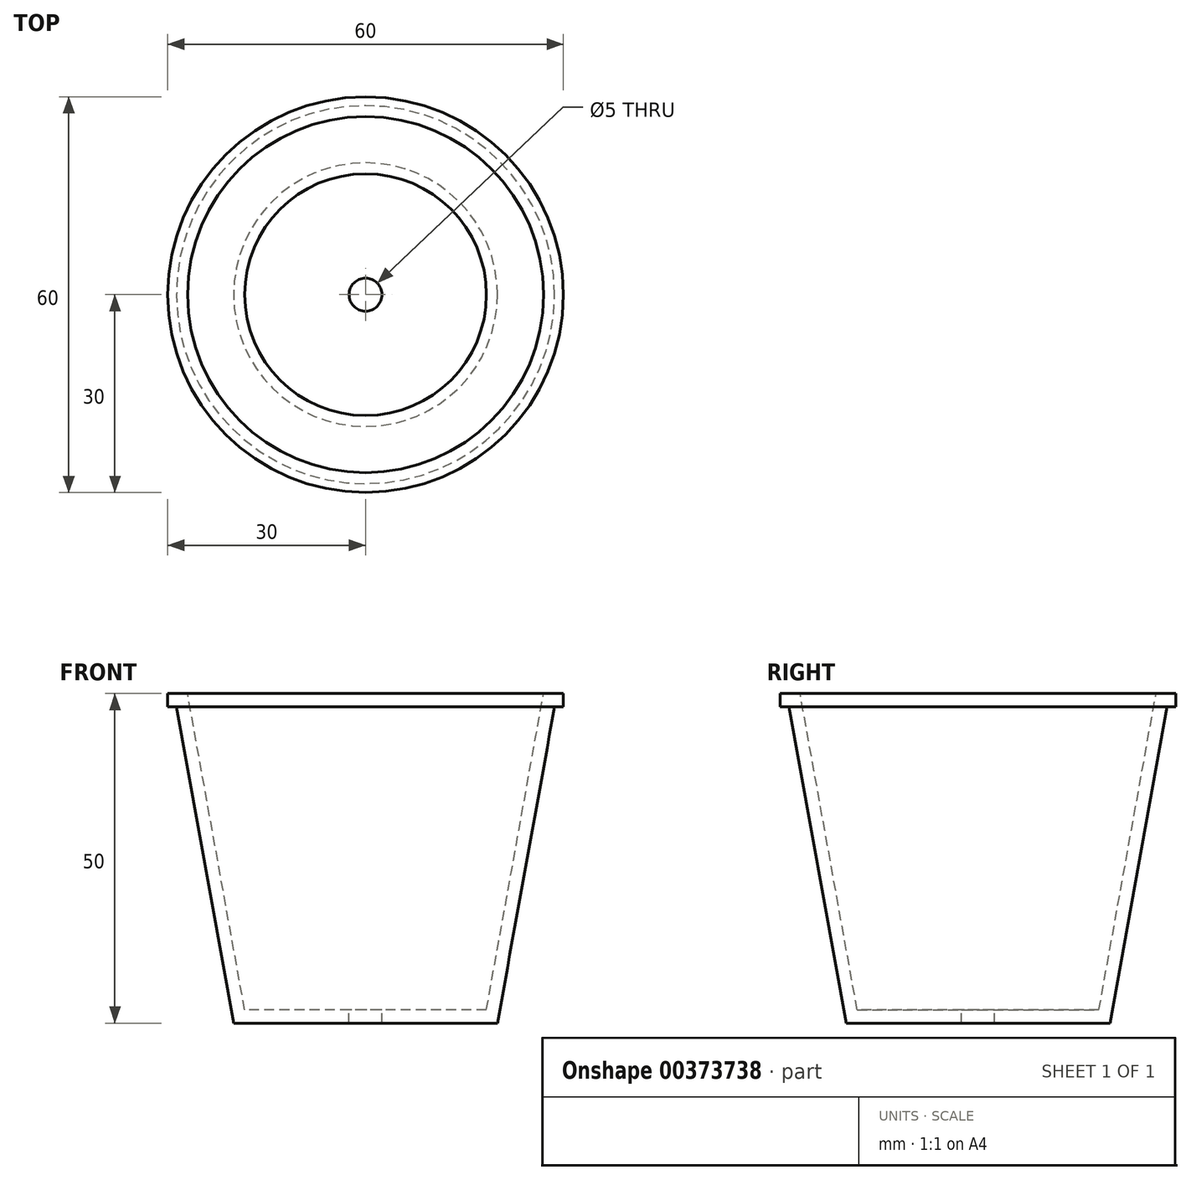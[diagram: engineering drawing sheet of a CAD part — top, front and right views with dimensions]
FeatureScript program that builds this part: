
annotation { "Feature Type Name" : "Feature", "Feature Type Description" : "" }
export const myFeature = defineFeature(function(context is Context, id is Id, definition is map)
    precondition{}
    {
        {
            var Q0;
            Q0=qCreatedBy(makeId("Front.planeOp"),FACE);
            var sketch = newSketch(context, id + "F0", { "sketchPlane" : qUnion([Q0])});
            skLineSegment(sketch, "E0", {"start": v(2.5, 2) * mm, "end": v(2.5, 0) * mm});
            skLineSegment(sketch, "E1", {"start": v(2.5, 0) * mm, "end": v(20, 0) * mm});
            skLineSegment(sketch, "E2", {"start": v(20, 0) * mm, "end": v(28.67, 48) * mm});
            skLineSegment(sketch, "E3", {"start": v(28.67, 48) * mm, "end": v(30, 48) * mm});
            skLineSegment(sketch, "E4", {"start": v(30, 48) * mm, "end": v(30, 50) * mm});
            skLineSegment(sketch, "E5", {"start": v(30, 50) * mm, "end": v(27, 50) * mm});
            skLineSegment(sketch, "E6", {"start": v(27, 50) * mm, "end": v(18.33, 2) * mm});
            skLineSegment(sketch, "E7", {"start": v(2.5, 2) * mm, "end": v(18.33, 2) * mm});
            skLineSegment(sketch, "E8", {"start": v(0, 0) * mm, "end": v(0, 49.42) * mm, "construction": true});
            skSolve(sketch);
        }
        {
            var Q0;
            Q0=sQuery(id+"F0.wireOp",EDGE,"E8");
            var Q1;
            Q1=sQuery(id+"F0.wireOp",EDGE,"E7");
            var Q2;
            Q2=sQuery(id+"F0.wireOp",EDGE,"E0");
            var Q3;
            Q3=sQuery(id+"F0.wireOp",EDGE,"E1");
            var Q4;
            Q4=sQuery(id+"F0.wireOp",EDGE,"E6");
            var Q5;
            Q5=sQuery(id+"F0.wireOp",EDGE,"E2");
            var Q6;
            Q6=sQuery(id+"F0.wireOp",EDGE,"E3");
            var Q7;
            Q7=sQuery(id+"F0.wireOp",EDGE,"E4");
            var Q8;
            Q8=sQuery(id+"F0.wireOp",EDGE,"E5");
            var Q9;
            Q9=sQuery(id+"F0.wireOp",EDGE,"E8");
            revolve(context, id + "F1", {"bodyType" : ToolBodyType.SURFACE, "surfaceEntities" : qUnion([Q0, Q1, Q2, Q3, Q4, Q5, Q6, Q7, Q8]), "axis" : qUnion([Q9]), "revolveType" : RevolveType.FULL});
        }
    });
